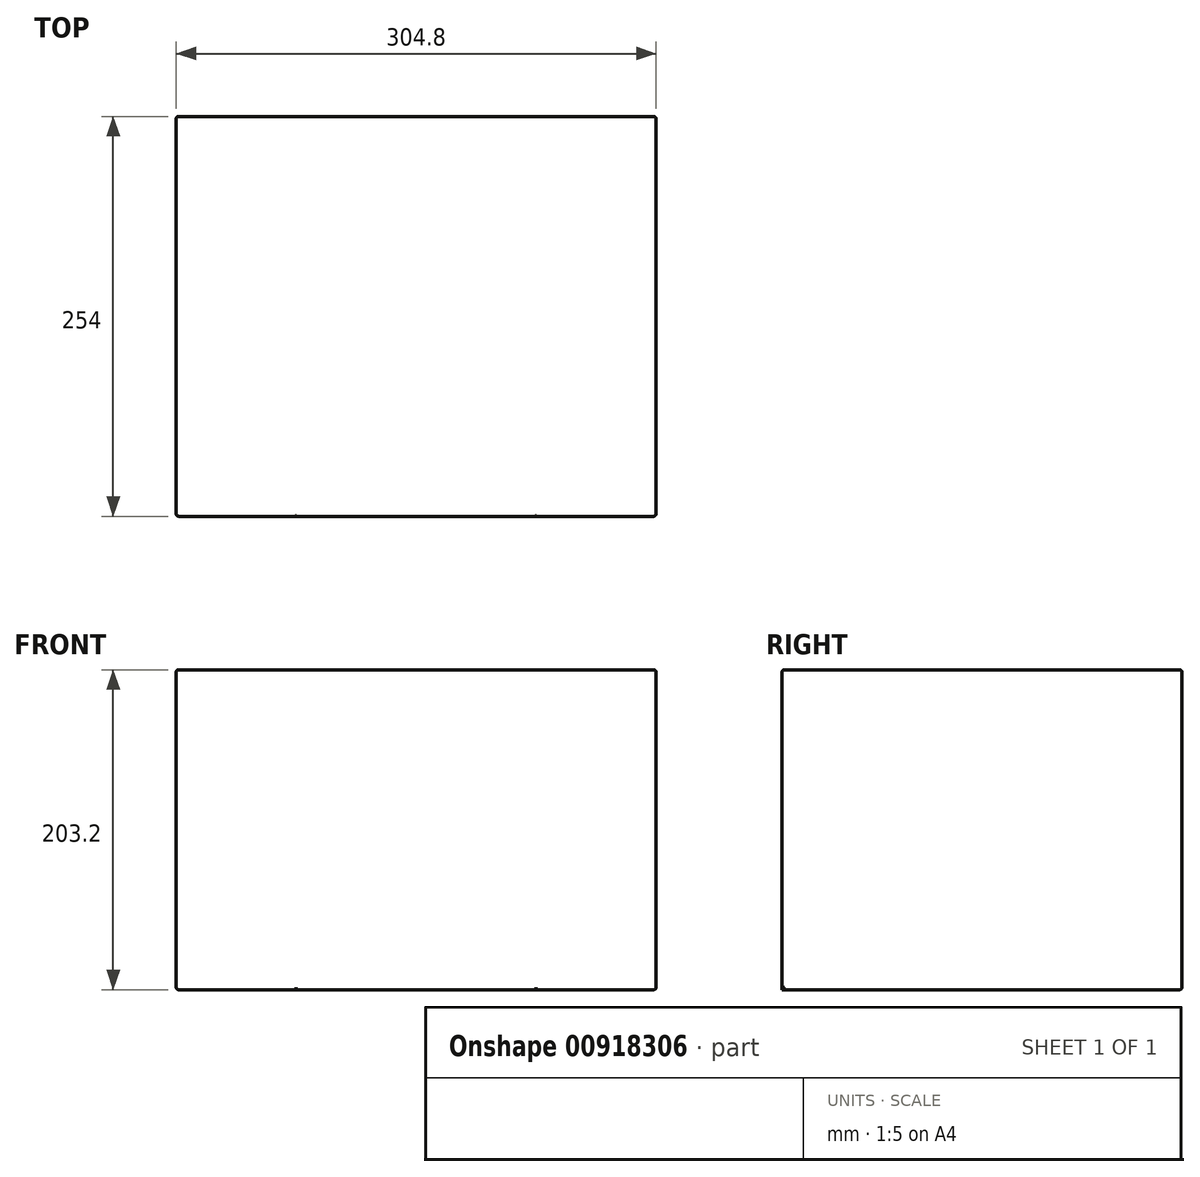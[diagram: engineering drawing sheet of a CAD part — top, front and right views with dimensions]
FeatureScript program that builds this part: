
annotation { "Feature Type Name" : "Feature", "Feature Type Description" : "" }
export const myFeature = defineFeature(function(context is Context, id is Id, definition is map)
    precondition{}
    {
        {
            var Q0;
            Q0=qCreatedBy(makeId("Front.planeOp"),FACE);
            var sketch = newSketch(context, id + "F0", { "sketchPlane" : qUnion([Q0])});
            skLineSegment(sketch, "E0.bottom", {"start": v(152.4, 127) * mm, "end": v(-152.4, 127) * mm});
            skLineSegment(sketch, "E0.top", {"start": v(152.4, -127) * mm, "end": v(-152.4, -127) * mm});
            skLineSegment(sketch, "E0.left", {"start": v(152.4, 127) * mm, "end": v(152.4, -127) * mm});
            skLineSegment(sketch, "E0.right", {"start": v(-152.4, 127) * mm, "end": v(-152.4, -127) * mm});
            skPoint(sketch, "E0.middle", {"position": v(0, 0) * mm});
            skLineSegment(sketch, "E1", {"start": v(-152.4, 0) * mm, "end": v(152.4, 0) * mm, "construction": true});
            skSolve(sketch);
        }
        {
            var Q0;
            Q0=makeQuery(id+"F0.imprint","IMPRINT",FACE,{"disambiguationData":[TD([[makeQuery(id+"F0.imprint","IMPRINT",EDGE,{"derivedFrom":sQuery(id+"F0.wireOp",EDGE,"E0.bottom")}),1.0]])]});
            extrude(context, id + "F1", {"entities" : qUnion([Q0]), "endBound" : BoundingType.SYMMETRIC, "depth" : 203.2 * mm, "offsetDistance" : 25.4 * mm});
        }
        {
            var Q0;
            Q0=makeQuery(id+"F1.opExtrude","SWEPT_FACE",FACE,{"disambiguationData":[OSD([sQuery(id+"F0.wireOp",EDGE,"E0.top")])]});
            var sketch = newSketch(context, id + "F2", { "sketchPlane" : qUnion([Q0])});
            skLineSegment(sketch, "E2.bottom", {"start": v(152.4, -101.6) * mm, "end": v(76.2, -101.6) * mm});
            skLineSegment(sketch, "E2.top", {"start": v(152.4, 0) * mm, "end": v(76.2, 0) * mm});
            skLineSegment(sketch, "E2.left", {"start": v(152.4, -101.6) * mm, "end": v(152.4, 0) * mm});
            skLineSegment(sketch, "E2.right", {"start": v(76.2, -101.6) * mm, "end": v(76.2, 0) * mm});
            skLineSegment(sketch, "E3", {"start": v(0, -101.6) * mm, "end": v(0, 101.6) * mm, "construction": true});
            skLineSegment(sketch, "E4.MirrorCS", {"start": v(-152.4, 0) * mm, "end": v(-76.2, 0) * mm});
            skLineSegment(sketch, "E5.MirrorCS", {"start": v(-152.4, -101.6) * mm, "end": v(-152.4, 0) * mm});
            skLineSegment(sketch, "E6.MirrorCS", {"start": v(-76.2, -101.6) * mm, "end": v(-76.2, 0) * mm});
            skLineSegment(sketch, "E7.MirrorCS", {"start": v(-152.4, -101.6) * mm, "end": v(-76.2, -101.6) * mm});
            skSolve(sketch);
        }
        {
            var Q0;
            Q0=makeQuery(id+"F2.imprint","IMPRINT",FACE,{"disambiguationData":[TD([[makeQuery(id+"F2.imprint","IMPRINT",EDGE,{"derivedFrom":sQuery(id+"F2.wireOp",EDGE,"E2.bottom")}),-1.0]])]});
            var Q1;
            Q1=makeQuery(id+"F2.imprint","IMPRINT",FACE,{"disambiguationData":[TD([[makeQuery(id+"F2.imprint","IMPRINT",EDGE,{"derivedFrom":sQuery(id+"F2.wireOp",EDGE,"E4.MirrorCS")}),-1.0]])]});
            extrude(context, id + "F3", {"entities" : qUnion([Q0, Q1]), "operationType" : NewBodyOperationType.REMOVE, "oppositeDirection" : true, "depth" : 25.4 * mm, "offsetDistance" : 25.4 * mm});
        }
        {
            var Q0;
            Q0=makeQuery(id+"F3.boolean.opBoolean","COPY",FACE,{"derivedFrom":makeQuery(id+"F3.opExtrude","CAP_FACE",FACE,{"disambiguationData":[OSD([sQuery(id+"F2.wireOp",EDGE,"E2.bottom"),sQuery(id+"F2.wireOp",EDGE,"E2.top"),sQuery(id+"F2.wireOp",EDGE,"E2.left"),sQuery(id+"F2.wireOp",EDGE,"E2.right")])],"isStart":false})});
            var Q1;
            Q1=makeQuery(id+"F3.boolean.opBoolean","COPY",FACE,{"derivedFrom":makeQuery(id+"F3.opExtrude","CAP_FACE",FACE,{"disambiguationData":[OSD([sQuery(id+"F2.wireOp",EDGE,"E4.MirrorCS"),sQuery(id+"F2.wireOp",EDGE,"E5.MirrorCS"),sQuery(id+"F2.wireOp",EDGE,"E6.MirrorCS"),sQuery(id+"F2.wireOp",EDGE,"E7.MirrorCS")])],"isStart":false})});
            extrude(context, id + "F4", {"entities" : qUnion([Q0, Q1]), "depth" : 25.4 * mm, "offsetDistance" : 25.4 * mm});
        }
        {
            var Q0;
            Q0=makeQuery(id+"F1.opExtrude","CAP_FACE",FACE,{"disambiguationData":[OSD([sQuery(id+"F0.wireOp",EDGE,"E0.bottom"),sQuery(id+"F0.wireOp",EDGE,"E0.top"),sQuery(id+"F0.wireOp",EDGE,"E0.left"),sQuery(id+"F0.wireOp",EDGE,"E0.right")])],"isStart":false});
            var Q1;
            Q1=makeQuery(id+"F1.opExtrude","SWEPT_FACE",FACE,{"disambiguationData":[OSD([sQuery(id+"F0.wireOp",EDGE,"E0.bottom")])]});
            var Q2;
            Q2=makeQuery(id+"F1.opExtrude","CAP_EDGE",EDGE,{"disambiguationData":[OSD([sQuery(id+"F0.wireOp",EDGE,"E0.left")])],"isStart":true});
            var Q3;
            Q3=makeQuery(id+"F4.opExtrude","SWEPT_EDGE",EDGE,{"disambiguationData":[OSD([sQuery(id+"F2.wireOp",EDGE,"E2.bottom"),sQuery(id+"F2.wireOp",EDGE,"E2.left")])]});
            var Q4;
            Q4=makeQuery(id+"F1.opExtrude","CAP_EDGE",EDGE,{"disambiguationData":[OSD([sQuery(id+"F0.wireOp",EDGE,"E0.right")])],"isStart":true});
            var Q5;
            Q5=makeQuery(id+"F4.opExtrude","SWEPT_EDGE",EDGE,{"disambiguationData":[OSD([sQuery(id+"F2.wireOp",EDGE,"E5.MirrorCS"),sQuery(id+"F2.wireOp",EDGE,"E7.MirrorCS")])]});
            var Q6;
            Q6=makeQuery(id+"F1.opExtrude","SWEPT_EDGE",EDGE,{"disambiguationData":[OSD([sQuery(id+"F0.wireOp",EDGE,"E0.top"),sQuery(id+"F0.wireOp",EDGE,"E0.right")])]});
            var Q7;
            Q7=makeQuery(id+"F4.opExtrude","CAP_EDGE",EDGE,{"disambiguationData":[OSD([sQuery(id+"F2.wireOp",EDGE,"E5.MirrorCS")])],"isStart":false});
            var Q8;
            Q8=makeQuery(id+"F4.opExtrude","CAP_EDGE",EDGE,{"disambiguationData":[OSD([sQuery(id+"F2.wireOp",EDGE,"E7.MirrorCS")])],"isStart":false});
            var Q9;
            Q9=makeQuery(id+"F1.opExtrude","CAP_EDGE",EDGE,{"disambiguationData":[OSD([sQuery(id+"F0.wireOp",EDGE,"E0.top")])],"isStart":true});
            var Q10;
            Q10=makeQuery(id+"F4.opExtrude","CAP_EDGE",EDGE,{"disambiguationData":[OSD([sQuery(id+"F2.wireOp",EDGE,"E2.bottom")])],"isStart":false});
            var Q11;
            Q11=makeQuery(id+"F4.opExtrude","CAP_EDGE",EDGE,{"disambiguationData":[OSD([sQuery(id+"F2.wireOp",EDGE,"E2.left")])],"isStart":false});
            var Q12;
            Q12=makeQuery(id+"F1.opExtrude","SWEPT_EDGE",EDGE,{"disambiguationData":[OSD([sQuery(id+"F0.wireOp",EDGE,"E0.top"),sQuery(id+"F0.wireOp",EDGE,"E0.left")])]});
            fillet(context, id + "F5", {"entities" : qUnion([Q0, Q1, Q2, Q3, Q4, Q5, Q6, Q7, Q8, Q9, Q10, Q11, Q12]), "radius" : 1.52 * mm, "tangentPropagation" : true, "allowEdgeOverflow" : false});
        }
        {
            var Q0;
            Q0=makeQuery(id+"F1.opExtrude","SWEPT_FACE",FACE,{"disambiguationData":[OSD([sQuery(id+"F0.wireOp",EDGE,"E0.left")])]});
            var sketch = newSketch(context, id + "F6", { "sketchPlane" : qUnion([Q0])});
            skLineSegment(sketch, "E8.bottom", {"start": v(100.08, -101.6) * mm, "end": v(23.88, -101.6) * mm});
            skLineSegment(sketch, "E8.top", {"start": v(100.08, -76.2) * mm, "end": v(23.88, -76.2) * mm});
            skLineSegment(sketch, "E8.left", {"start": v(100.08, -101.6) * mm, "end": v(100.08, -76.2) * mm});
            skLineSegment(sketch, "E8.right", {"start": v(23.88, -101.6) * mm, "end": v(23.88, -76.2) * mm});
            skSolve(sketch);
        }
        {
            var Q0;
            Q0=makeQuery(id+"F6.imprint","IMPRINT",FACE,{"disambiguationData":[TD([[makeQuery(id+"F6.imprint","IMPRINT",EDGE,{"derivedFrom":sQuery(id+"F6.wireOp",EDGE,"E8.bottom")}),1.0]])]});
            extrude(context, id + "F7", {"entities" : qUnion([Q0]), "operationType" : NewBodyOperationType.REMOVE, "oppositeDirection" : true, "depth" : 25.4 * mm, "offsetDistance" : 25.4 * mm});
        }
        {
            var Q0;
            Q0=makeQuery(id+"F7.boolean.opBoolean","COPY",FACE,{"derivedFrom":makeQuery(id+"F7.opExtrude","CAP_FACE",FACE,{"disambiguationData":[OSD([sQuery(id+"F6.wireOp",EDGE,"E8.bottom"),sQuery(id+"F6.wireOp",EDGE,"E8.top"),sQuery(id+"F6.wireOp",EDGE,"E8.left"),sQuery(id+"F6.wireOp",EDGE,"E8.right")])],"isStart":false})});
            extrude(context, id + "F8", {"entities" : qUnion([Q0]), "operationType" : NewBodyOperationType.ADD, "depth" : 25.4 * mm, "offsetDistance" : 25.4 * mm});
        }
        {
            var Q0;
            Q0=makeQuery(id+"F1.opExtrude","SWEPT_FACE",FACE,{"disambiguationData":[OSD([sQuery(id+"F0.wireOp",EDGE,"E0.right")])]});
            var sketch = newSketch(context, id + "F9", { "sketchPlane" : qUnion([Q0])});
            skLineSegment(sketch, "E9.0", {"start": v(-100.08, -101.6) * mm, "end": v(-100.08, -76.2) * mm});
            skLineSegment(sketch, "E10.0", {"start": v(-100.08, -76.2) * mm, "end": v(-23.88, -76.2) * mm});
            skLineSegment(sketch, "E11.0", {"start": v(-100.08, -101.6) * mm, "end": v(-23.88, -101.6) * mm});
            skLineSegment(sketch, "E12.0", {"start": v(-23.88, -101.6) * mm, "end": v(-23.88, -76.2) * mm});
            skSolve(sketch);
        }
        {
            var Q0;
            Q0=makeQuery(id+"F9.imprint","IMPRINT",FACE,{"disambiguationData":[TD([[makeQuery(id+"F9.imprint","IMPRINT",EDGE,{"derivedFrom":sQuery(id+"F9.wireOp",EDGE,"E9.0")}),1.0]])]});
            extrude(context, id + "F10", {"entities" : qUnion([Q0]), "operationType" : NewBodyOperationType.REMOVE, "oppositeDirection" : true, "depth" : 25.4 * mm, "offsetDistance" : 25.4 * mm});
        }
        {
            var Q0;
            Q0=makeQuery(id+"F10.boolean.opBoolean","COPY",FACE,{"derivedFrom":makeQuery(id+"F10.opExtrude","CAP_FACE",FACE,{"disambiguationData":[OSD([sQuery(id+"F9.wireOp",EDGE,"E9.0"),sQuery(id+"F9.wireOp",EDGE,"E10.0"),sQuery(id+"F9.wireOp",EDGE,"E11.0"),sQuery(id+"F9.wireOp",EDGE,"E12.0")])],"isStart":false})});
            extrude(context, id + "F11", {"entities" : qUnion([Q0]), "operationType" : NewBodyOperationType.ADD, "depth" : 25.4 * mm, "offsetDistance" : 25.4 * mm});
        }
        {
            var Q0;
            Q0=makeQuery(id+"F4.opExtrude","SWEPT_BODY",BODY,{"disambiguationData":[OSD([sQuery(id+"F2.wireOp",EDGE,"E2.bottom"),sQuery(id+"F2.wireOp",EDGE,"E2.top"),sQuery(id+"F2.wireOp",EDGE,"E2.left"),sQuery(id+"F2.wireOp",EDGE,"E2.right")])]});
            var Q1;
            Q1=makeQuery(id+"F1.opExtrude","SWEPT_BODY",BODY,{"disambiguationData":[OSD([sQuery(id+"F0.wireOp",EDGE,"E0.bottom"),sQuery(id+"F0.wireOp",EDGE,"E0.top"),sQuery(id+"F0.wireOp",EDGE,"E0.left"),sQuery(id+"F0.wireOp",EDGE,"E0.right")])]});
            var Q2;
            Q2=makeQuery(id+"F4.opExtrude","SWEPT_BODY",BODY,{"disambiguationData":[OSD([sQuery(id+"F2.wireOp",EDGE,"E4.MirrorCS"),sQuery(id+"F2.wireOp",EDGE,"E5.MirrorCS"),sQuery(id+"F2.wireOp",EDGE,"E6.MirrorCS"),sQuery(id+"F2.wireOp",EDGE,"E7.MirrorCS")])]});
            var Q3;
            Q3=sQuery(id+"F0.wireOp",EDGE,"E1");
            transform(context, id + "F12", {"entities" : qUnion([Q0, Q1, Q2]), "transformType" : TransformType.ROTATION, "transformAxis" : qUnion([Q3]), "angle" : 90 * degree, "oppositeDirection" : true, "makeCopy" : false});
        }
    });
